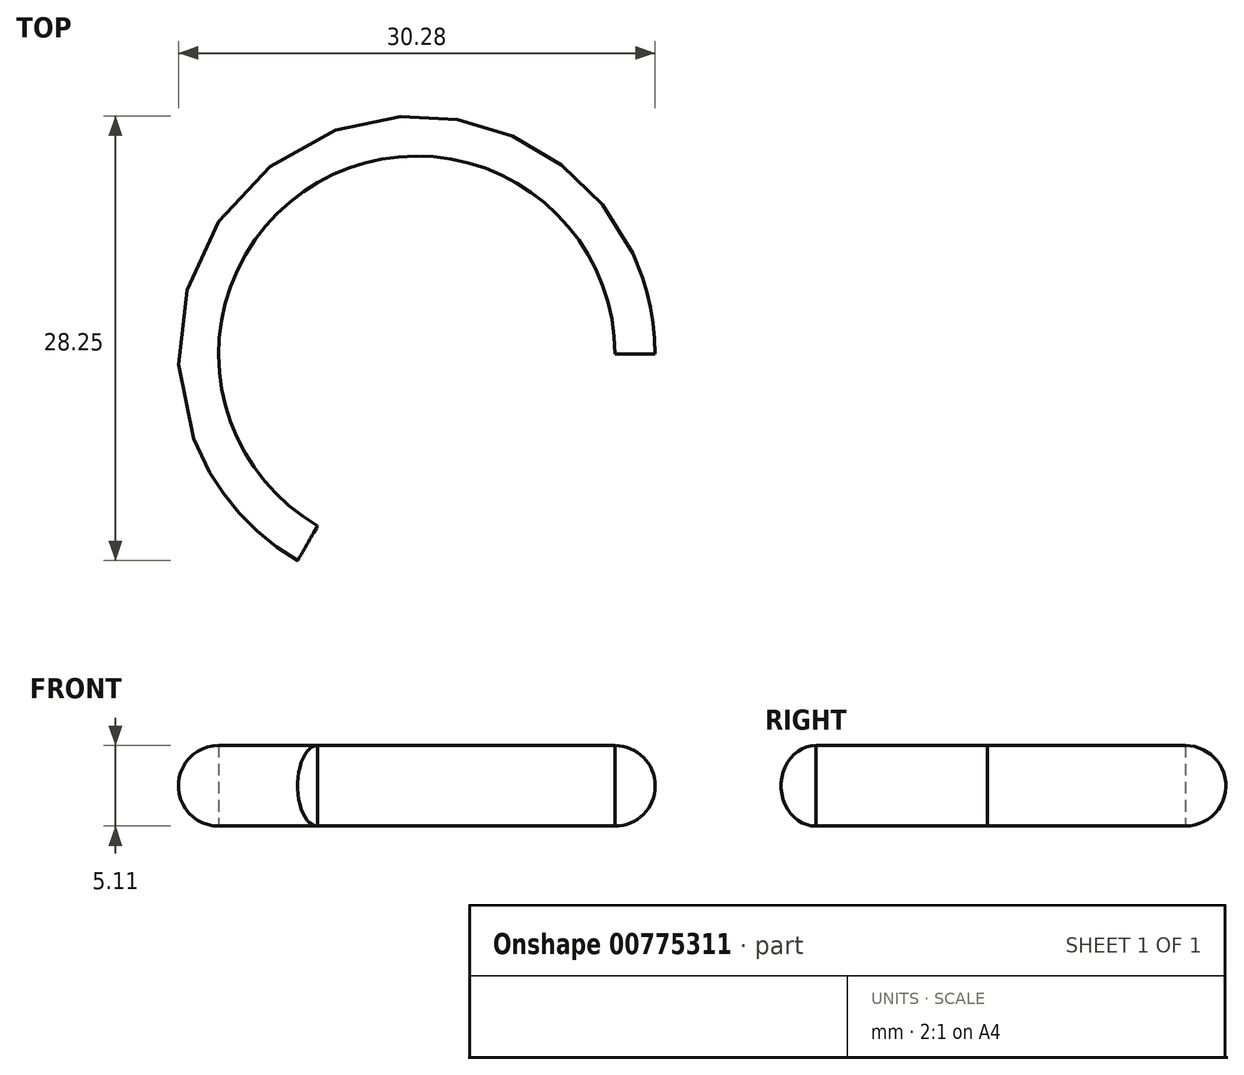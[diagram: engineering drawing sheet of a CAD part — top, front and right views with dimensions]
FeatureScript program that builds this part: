
annotation { "Feature Type Name" : "Feature", "Feature Type Description" : "" }
export const myFeature = defineFeature(function(context is Context, id is Id, definition is map)
    precondition{}
    {
        {
            var Q0;
            Q0=qCreatedBy(makeId("Front.planeOp"),FACE);
            var sketch = newSketch(context, id + "F0", { "sketchPlane" : qUnion([Q0])});
            skLineSegment(sketch, "E0", {"start": v(50.27, 0) * mm, "end": v(37.68, 0) * mm});
            skLineSegment(sketch, "E1", {"start": v(37.68, 0) * mm, "end": v(37.68, 11.52) * mm});
            skLineSegment(sketch, "E2", {"start": v(50.27, 0) * mm, "end": v(50.27, 5.11) * mm});
            skArc(sketch, "E3", {"start": v(50.27, 0) * mm, "mid": v(52.82, 2.55) * mm, "end": v(50.27, 5.11) * mm});
            skSolve(sketch);
        }
        {
            var Q0;
            Q0 = qSketchRegion(id + "F0", true);
            var Q1;
            Q1=sQuery(id+"F0.wireOp",EDGE,"E1");
            revolve(context, id + "F1", {"surfaceOperationType" : NewSurfaceOperationType.NEW, "entities" : qUnion([Q0]), "axis" : qUnion([Q1]), "revolveType" : RevolveType.ONE_DIRECTION, "angle" : 240 * degree});
        }
    });
